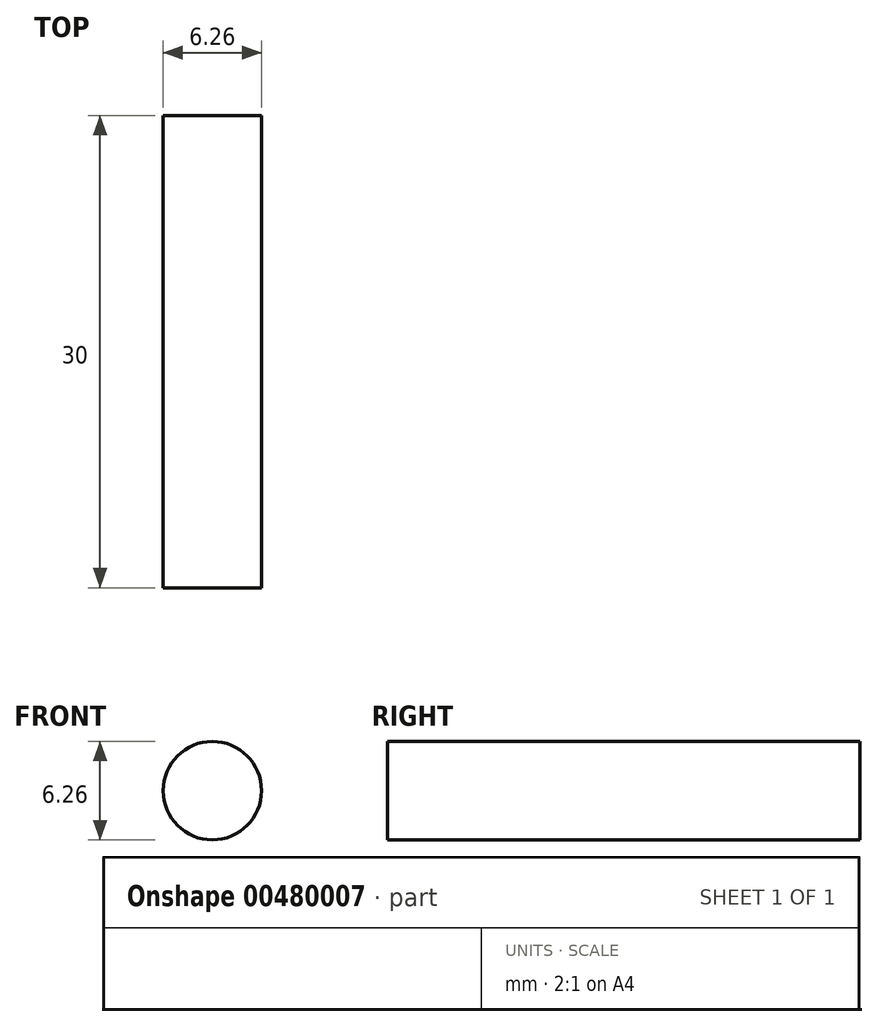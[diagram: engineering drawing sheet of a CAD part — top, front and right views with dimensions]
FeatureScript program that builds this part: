
annotation { "Feature Type Name" : "Feature", "Feature Type Description" : "" }
export const myFeature = defineFeature(function(context is Context, id is Id, definition is map)
    precondition{}
    {
        {
            var Q0;
            Q0=qCreatedBy(makeId("Front.planeOp"),FACE);
            var sketch = newSketch(context, id + "F0", { "sketchPlane" : qUnion([Q0])});
            skCircle(sketch, "E0", {"center": v(0, 0) * mm, "radius": 3.12 * mm});
            skSolve(sketch);
        }
        {
            var Q0;
            Q0=makeQuery(id+"F0.imprint","IMPRINT",FACE,{"disambiguationData":[TD([[makeQuery(id+"F0.imprint","IMPRINT",EDGE,{"derivedFrom":sQuery(id+"F0.wireOp",EDGE,"E0")}),1.0]])]});
            extrude(context, id + "F1", {"entities" : qUnion([Q0]), "depth" : 30 * mm});
        }
    });
